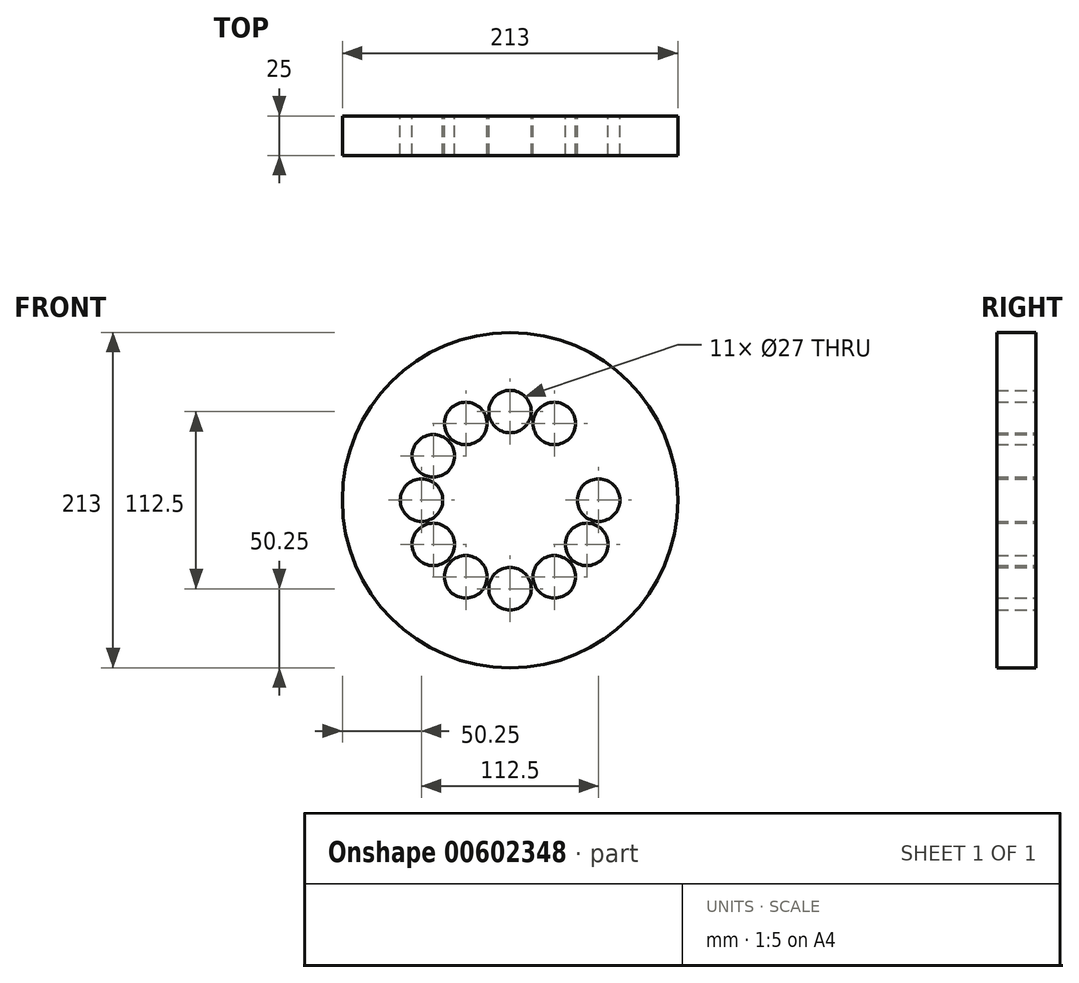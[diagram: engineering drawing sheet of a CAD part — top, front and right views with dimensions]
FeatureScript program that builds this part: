
annotation { "Feature Type Name" : "Feature", "Feature Type Description" : "" }
export const myFeature = defineFeature(function(context is Context, id is Id, definition is map)
    precondition{}
    {
        {
            var Q0;
            Q0=qCreatedBy(makeId("Front.planeOp"),FACE);
            var sketch = newSketch(context, id + "F0", { "sketchPlane" : qUnion([Q0])});
            skCircle(sketch, "E0", {"center": v(0, 0) * mm, "radius": 32.5 * mm});
            skCircle(sketch, "E1", {"center": v(0, 0) * mm, "radius": 37.5 * mm});
            skCircle(sketch, "E2", {"center": v(0, 0) * mm, "radius": 75 * mm});
            skCircle(sketch, "E3", {"center": v(0, 0) * mm, "radius": 106.5 * mm});
            skPoint(sketch, "E4.orphan", {"position": v(0, 106.5) * mm});
            skCircle(sketch, "E5", {"center": v(0, 56.25) * mm, "radius": 13.5 * mm});
            skCircle(sketch, "E6", {"center": v(-56.25, 0) * mm, "radius": 13.5 * mm});
            skPoint(sketch, "E6.centerSnap0", {"position": v(-53.25, 0) * mm});
            skCircle(sketch, "E7", {"center": v(0, -56.25) * mm, "radius": 13.5 * mm});
            skCircle(sketch, "E8", {"center": v(56.25, 0) * mm, "radius": 13.5 * mm});
            skCircle(sketch, "E9", {"center": v(-48.71, 28.12) * mm, "radius": 13.5 * mm});
            skCircle(sketch, "E10", {"center": v(-28.13, 48.71) * mm, "radius": 13.5 * mm});
            skCircle(sketch, "E11", {"center": v(-48.71, -28.13) * mm, "radius": 13.5 * mm});
            skCircle(sketch, "E12", {"center": v(-28.12, -48.71) * mm, "radius": 13.5 * mm});
            skCircle(sketch, "E13", {"center": v(28.12, 48.71) * mm, "radius": 13.5 * mm});
            skCircle(sketch, "E14", {"center": v(28.13, -48.71) * mm, "radius": 13.5 * mm});
            skCircle(sketch, "E15", {"center": v(48.71, -28.12) * mm, "radius": 13.5 * mm});
            skSolve(sketch);
        }
        {
            var Q0;
            Q0 = qSketchRegion(id + "F0", true);
            var Q1;
            Q1=makeQuery(id+"F0.imprint","IMPRINT",FACE,{"disambiguationData":[TD([[makeQuery(id+"F0.imprint","IMPRINT",EDGE,{"derivedFrom":sQuery(id+"F0.wireOp",EDGE,"E0")}),1.0]])]});
            var Q2;
            Q2=makeQuery(id+"F0.imprint","IMPRINT",FACE,{"disambiguationData":[TD([[makeQuery(id+"F0.imprint","IMPRINT",EDGE,{"derivedFrom":sQuery(id+"F0.wireOp",EDGE,"E0")}),-1.0]])]});
            var Q3;
            Q3=makeQuery(id+"F0.imprint","IMPRINT",FACE,{"disambiguationData":[TD([[makeQuery(id+"F0.imprint","IMPRINT",EDGE,{"derivedFrom":sQuery(id+"F0.wireOp",EDGE,"E1")}),-1.0]])]});
            extrude(context, id + "F1", {"entities" : qUnion([Q0, Q1, Q2, Q3]), "depth" : 25 * mm, "offsetDistance" : 25 * mm});
        }
    });
